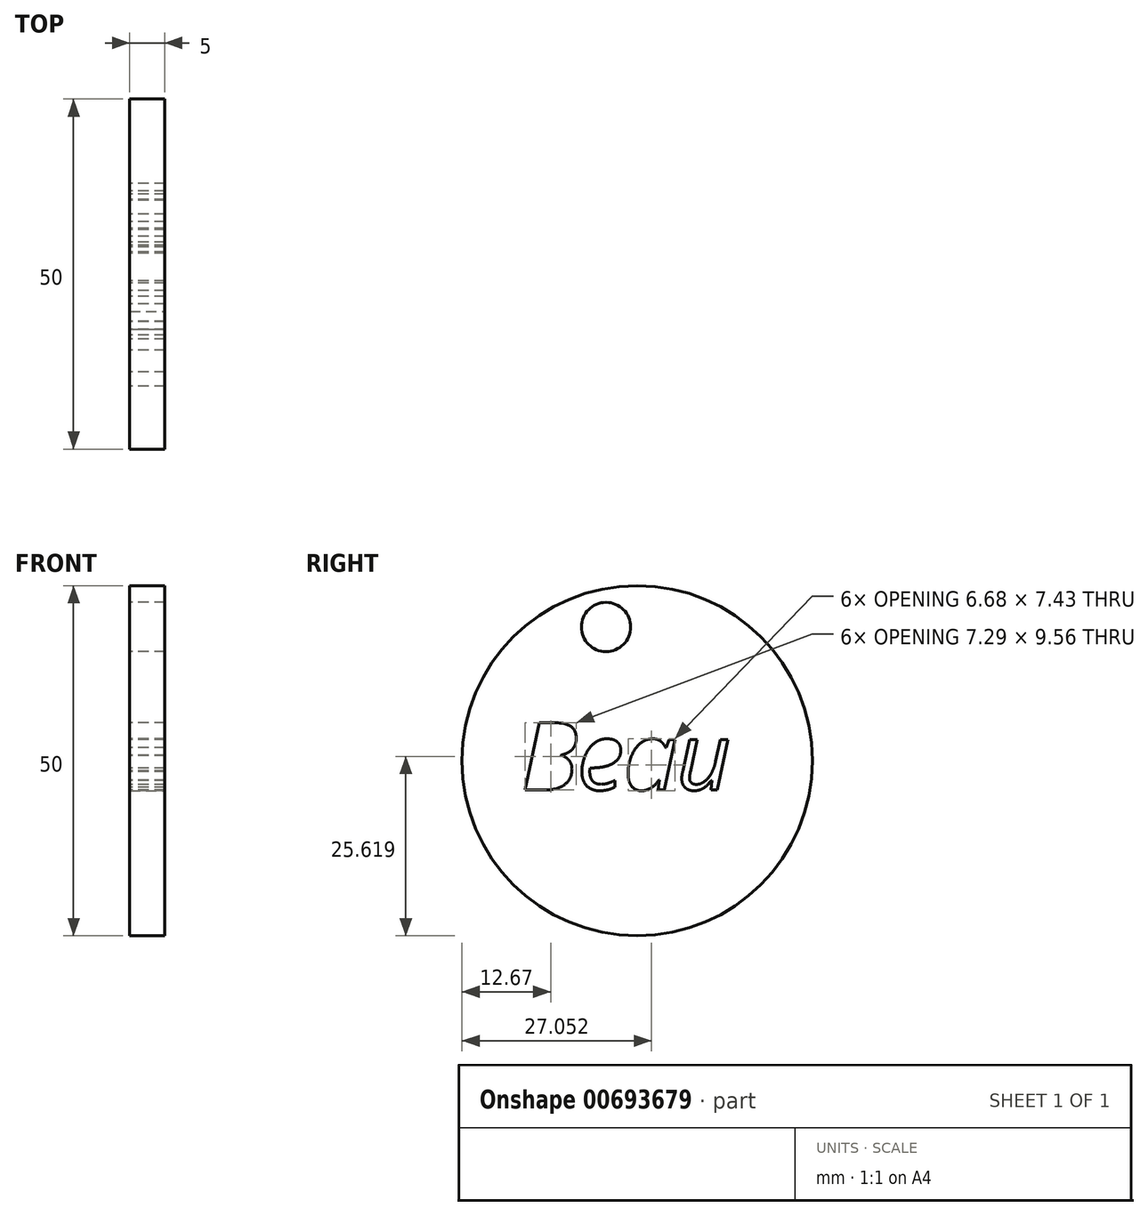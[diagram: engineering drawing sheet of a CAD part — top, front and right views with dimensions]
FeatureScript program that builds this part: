
annotation { "Feature Type Name" : "Feature", "Feature Type Description" : "" }
export const myFeature = defineFeature(function(context is Context, id is Id, definition is map)
    precondition{}
    {
        {
            var Q0;
            Q0=qCreatedBy(makeId("Right.planeOp"),FACE);
            var sketch = newSketch(context, id + "F0", { "sketchPlane" : qUnion([Q0])});
            skCircle(sketch, "E0", {"center": v(0, 0) * mm, "radius": 25 * mm});
            skText(sketch, "E1", { "text": "Beau", "fontName": "OpenSans-Italic.ttf"});
            skCircle(sketch, "E2", {"center": v(-4.44, 19.1) * mm, "radius": 3.52 * mm});
            const initialGuessF0  = {"E1": [-0.01654, -0.00416, 1, 0, 0.00964]};
            skSetInitialGuess(sketch, initialGuessF0);
            skSolve(sketch);
        }
        {
            var Q0;
            Q0=makeQuery(id+"F0.imprint","IMPRINT",FACE,{"disambiguationData":[TD([[makeQuery(id+"F0.imprint","IMPRINT",EDGE,{"derivedFrom":sQuery(id+"F0.wireOp",EDGE,"E0")}),1.0]])]});
            extrude(context, id + "F1", {"entities" : qUnion([Q0]), "depth" : 5 * mm, "offsetDistance" : 25 * mm});
        }
    });
